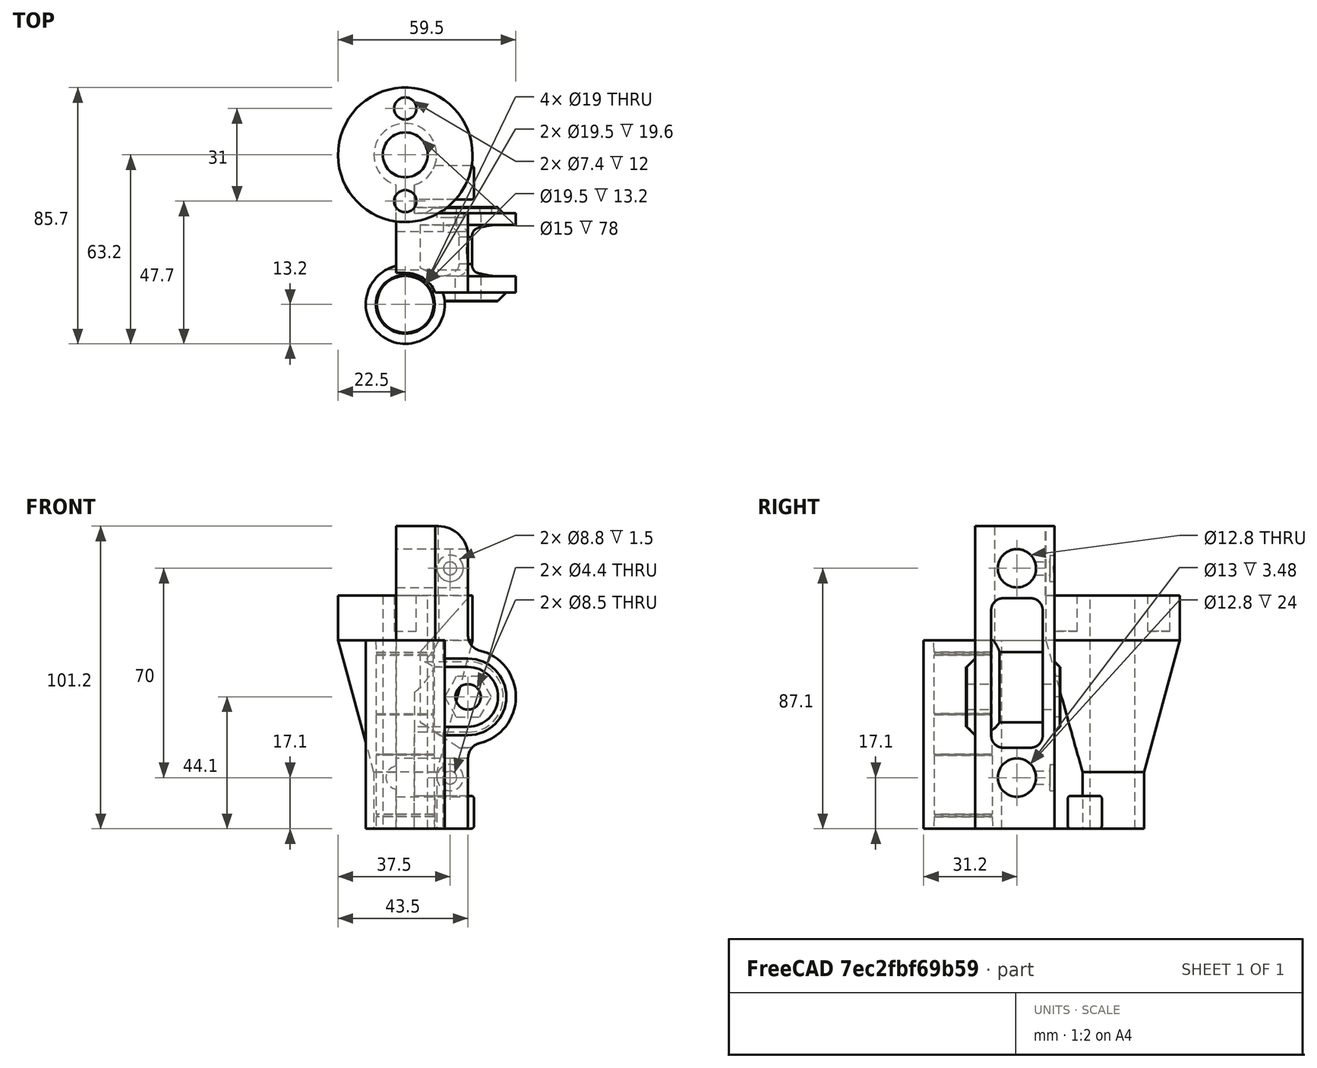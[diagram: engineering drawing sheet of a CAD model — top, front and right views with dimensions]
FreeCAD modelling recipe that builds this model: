
FCSTD DOCUMENT  (FreeCAD 0.17R7631 (Git))
Label: z_carriage_idler_v2.9.1
License: All rights reserved
LicenseURL: http://en.wikipedia.org/wiki/All_rights_reserved
objects: App::FeaturePython×12, Part::FeaturePython×3, Part::Fuse×2
note: 5 computed .brp shape members not serialized (recipe doc carries the construction recipe); baked Part::Feature solids carry a one-line shape summary decoded from their .brp

FEATURE [Part::FeaturePython] carriage_base_olive_idler_01  # a2plus imported part (geometry in sourceFile) (typed FeaturePython)
  Placement = pos=(0,0,0) rot=(1,0,0;1.5708rad)
  fixedPosition = true
  sourceFile = <userpath>/shared-j/devel/lulzbot/TAZ/Olive/production_parts/printed_parts/z_carriage_idler/carriage_base_olive_idler.fcstd
  timeLastImport = 1463595950
  updateColors = true
FEATURE [Part::FeaturePython] idler_switch_olive_extension_01  # a2plus imported part (geometry in sourceFile) (typed FeaturePython)
  Placement = pos=(0,0,0) rot=(0,0,-1;1.5708rad)
  fixedPosition = false
  sourceFile = <userpath>/shared-j/devel/lulzbot/TAZ/Olive/production_parts/printed_parts/z_carriage_idler/idler_switch_olive_extension.fcstd
  timeLastImport = 1460995200
  updateColors = true
FEATURE [App::FeaturePython] axialConstraint01  # a2plus constraint (typed FeaturePython)
  Object1 = carriage_base_olive_idler_01
  Object2 = z_idler_body_olive_exten_01001
  SubElement1 = Face24
  SubElement2 = Face22
  Type = axial
  directionConstraint = 1
  lockRotation = false
FEATURE [App::FeaturePython] axialConstraint01_mirror  label="axialConstraint01_"  # a2plus constraint (typed FeaturePython)
  Object1 = carriage_base_olive_idler_01
  Object2 = z_idler_body_olive_exten_01001
  SubElement1 = Face24
  SubElement2 = Face22
  Type = axial
  directionConstraint = 1
  lockRotation = false
FEATURE [App::FeaturePython] planeConstraint01  # a2plus constraint (typed FeaturePython)
  Object1 = carriage_base_olive_idler_01
  Object2 = z_idler_body_olive_exten_01001
  SubElement1 = Face20
  SubElement2 = Face20
  Type = plane
  directionConstraint = 1
  offset = 0
FEATURE [App::FeaturePython] planeConstraint01_mirror  label="planeConstraint01_"  # a2plus constraint (typed FeaturePython)
  Object1 = carriage_base_olive_idler_01
  Object2 = z_idler_body_olive_exten_01001
  SubElement1 = Face20
  SubElement2 = Face20
  Type = plane
  directionConstraint = 1
  offset = 0
FEATURE [App::FeaturePython] axialConstraint02  # a2plus constraint (typed FeaturePython)
  Object1 = idler_switch_olive_extension_01
  Object2 = carriage_base_olive_idler_01
  SubElement1 = Face1
  SubElement2 = Face25
  Type = axial
  directionConstraint = 0
  lockRotation = false
FEATURE [App::FeaturePython] axialConstraint02_mirror  label="axialConstraint02_"  # a2plus constraint (typed FeaturePython)
  Object1 = idler_switch_olive_extension_01
  Object2 = carriage_base_olive_idler_01
  SubElement1 = Face1
  SubElement2 = Face25
  Type = axial
  directionConstraint = 0
  lockRotation = false
FEATURE [App::FeaturePython] planeConstraint02  # a2plus constraint (typed FeaturePython)
  Object1 = idler_switch_olive_extension_01
  Object2 = carriage_base_olive_idler_01
  SubElement1 = Face5
  SubElement2 = Face33
  Type = plane
  directionConstraint = 0
  offset = 0
FEATURE [App::FeaturePython] planeConstraint02_mirror  label="planeConstraint02_"  # a2plus constraint (typed FeaturePython)
  Object1 = idler_switch_olive_extension_01
  Object2 = carriage_base_olive_idler_01
  SubElement1 = Face5
  SubElement2 = Face33
  Type = plane
  directionConstraint = 0
  offset = 0
FEATURE [Part::FeaturePython] z_idler_body_olive_exten_01  # a2plus imported part (geometry in sourceFile) (typed FeaturePython)
  Placement = pos=(21,-20.5,47.1) rot=(1,0,0;1.5708rad)
  fixedPosition = false
  sourceFile = <userpath>/shared-j/devel/lulzbot/TAZ/Olive/production_parts/printed_parts/z_carriage_idler/z_idler_body_olive_exten.fcstd
  timeLastImport = 1463596215
  updateColors = true
FEATURE [App::FeaturePython] planeConstraint03  # a2plus constraint (typed FeaturePython)
  Object1 = z_idler_body_olive_exten_01
  Object2 = z_idler_body_olive_exten_01001
  SubElement1 = Face8
  SubElement2 = Face8
  Type = plane
  directionConstraint = 0
  offset = 0
FEATURE [App::FeaturePython] planeConstraint03_mirror  label="planeConstraint03_"  # a2plus constraint (typed FeaturePython)
  Object1 = z_idler_body_olive_exten_01
  Object2 = z_idler_body_olive_exten_01001
  SubElement1 = Face8
  SubElement2 = Face8
  Type = plane
  directionConstraint = 0
  offset = 0
FEATURE [App::FeaturePython] axialConstraint03  # a2plus constraint (typed FeaturePython)
  Object1 = z_idler_body_olive_exten_01
  Object2 = z_idler_body_olive_exten_01001
  SubElement1 = Face22
  SubElement2 = Face22
  Type = axial
  directionConstraint = 0
  lockRotation = false
FEATURE [App::FeaturePython] axialConstraint03_mirror  label="axialConstraint03_"  # a2plus constraint (typed FeaturePython)
  Object1 = z_idler_body_olive_exten_01
  Object2 = z_idler_body_olive_exten_01001
  SubElement1 = Face22
  SubElement2 = Face22
  Type = axial
  directionConstraint = 0
  lockRotation = false
FEATURE [Part::Fuse] Fusion
  Base = -> carriage_base_olive_idler_01
  Tool = -> idler_switch_olive_extension_01
FEATURE [Part::Fuse] Fusion001
  Base = -> Fusion
  Tool = -> z_idler_body_olive_exten_01
